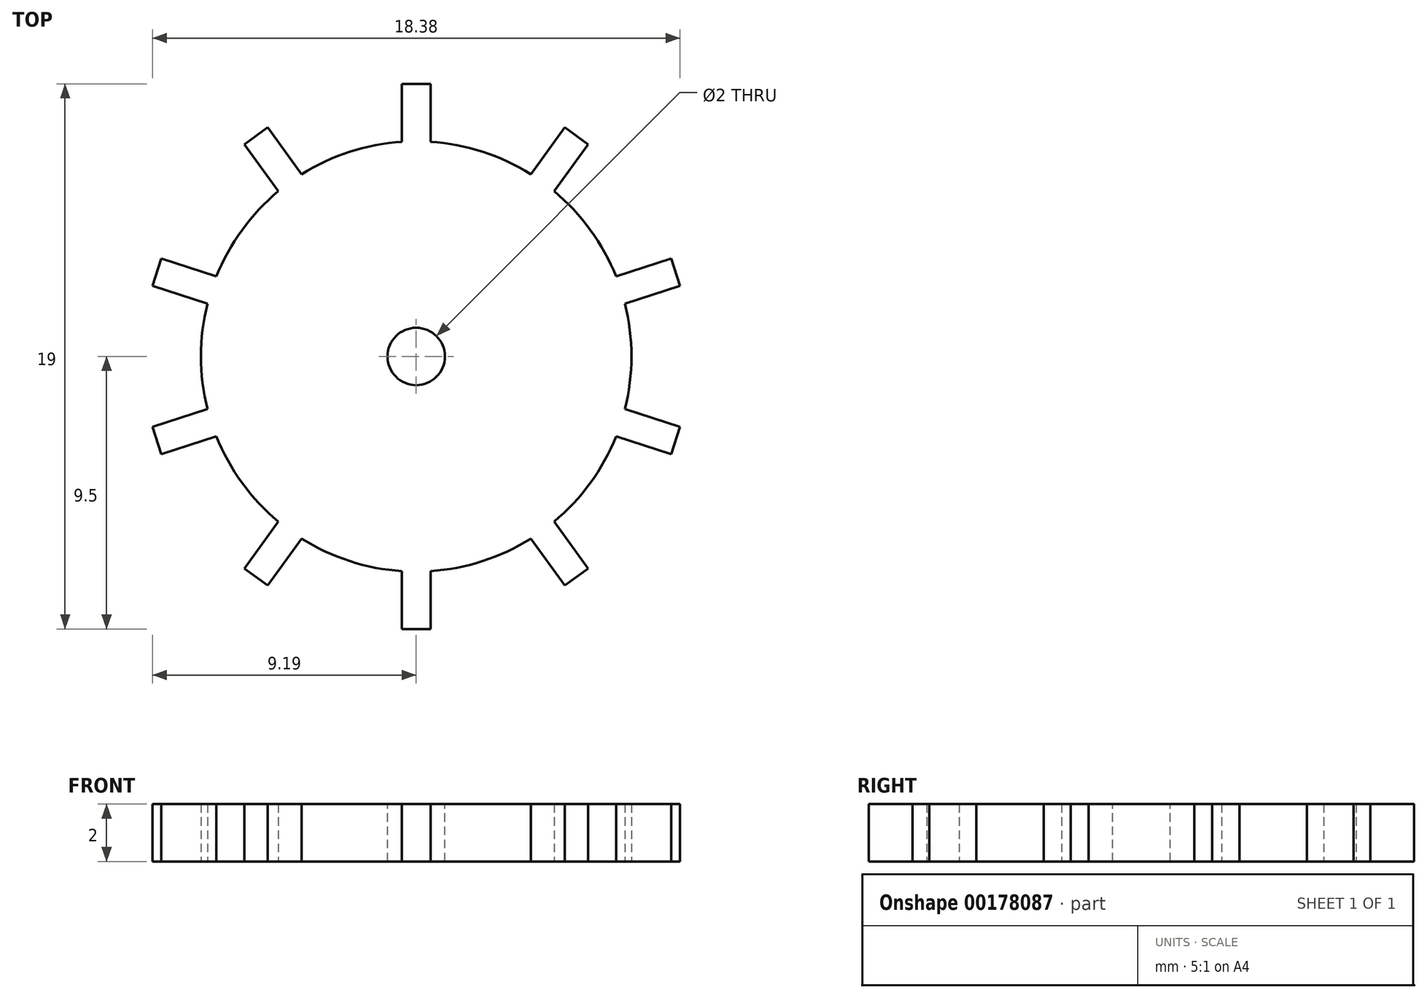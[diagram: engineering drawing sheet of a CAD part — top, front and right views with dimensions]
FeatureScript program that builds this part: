
annotation { "Feature Type Name" : "Feature", "Feature Type Description" : "" }
export const myFeature = defineFeature(function(context is Context, id is Id, definition is map)
    precondition{}
    {
        {
            var Q0;
            Q0=qCreatedBy(makeId("Top.planeOp"),FACE);
            var sketch = newSketch(context, id + "F0", { "sketchPlane" : qUnion([Q0])});
            skCircle(sketch, "E0", {"center": v(0, 0) * mm, "radius": 7.5 * mm});
            skLineSegment(sketch, "E1", {"start": v(0, 0) * mm, "end": v(0, 7.5) * mm, "construction": true});
            skLineSegment(sketch, "E2", {"start": v(0, 9.5) * mm, "end": v(-0.5, 9.5) * mm});
            skLineSegment(sketch, "E3", {"start": v(-0.5, 9.5) * mm, "end": v(-0.5, 7.48) * mm});
            skLineSegment(sketch, "E4.MirrorCS", {"start": v(0, 9.5) * mm, "end": v(0.5, 9.5) * mm});
            skLineSegment(sketch, "E5.MirrorCS", {"start": v(0.5, 9.5) * mm, "end": v(0.5, 7.48) * mm});
            skLineSegment(sketch, "E6.1.0", {"start": v(-5.99, 7.4) * mm, "end": v(-4.8, 5.76) * mm});
            skLineSegment(sketch, "E6.1.1", {"start": v(-5.58, 7.69) * mm, "end": v(-5.99, 7.4) * mm});
            skLineSegment(sketch, "E6.1.2", {"start": v(-5.58, 7.69) * mm, "end": v(-5.18, 7.98) * mm});
            skLineSegment(sketch, "E6.1.3", {"start": v(-5.18, 7.98) * mm, "end": v(-4, 6.35) * mm});
            skLineSegment(sketch, "E6.2.0", {"start": v(-9.19, 2.46) * mm, "end": v(-7.27, 1.84) * mm});
            skLineSegment(sketch, "E6.2.1", {"start": v(-9.04, 2.94) * mm, "end": v(-9.19, 2.46) * mm});
            skLineSegment(sketch, "E6.2.2", {"start": v(-9.04, 2.94) * mm, "end": v(-8.88, 3.41) * mm});
            skLineSegment(sketch, "E6.2.3", {"start": v(-8.88, 3.41) * mm, "end": v(-6.96, 2.79) * mm});
            skLineSegment(sketch, "E6.3.0", {"start": v(-8.88, -3.41) * mm, "end": v(-6.96, -2.79) * mm});
            skLineSegment(sketch, "E6.3.1", {"start": v(-9.04, -2.94) * mm, "end": v(-8.88, -3.41) * mm});
            skLineSegment(sketch, "E6.3.2", {"start": v(-9.04, -2.94) * mm, "end": v(-9.19, -2.46) * mm});
            skLineSegment(sketch, "E6.3.3", {"start": v(-9.19, -2.46) * mm, "end": v(-7.27, -1.84) * mm});
            skLineSegment(sketch, "E6.4.0", {"start": v(-5.18, -7.98) * mm, "end": v(-4, -6.35) * mm});
            skLineSegment(sketch, "E6.4.1", {"start": v(-5.58, -7.69) * mm, "end": v(-5.18, -7.98) * mm});
            skLineSegment(sketch, "E6.4.2", {"start": v(-5.58, -7.69) * mm, "end": v(-5.99, -7.4) * mm});
            skLineSegment(sketch, "E6.4.3", {"start": v(-5.99, -7.4) * mm, "end": v(-4.8, -5.76) * mm});
            skLineSegment(sketch, "E6.5.0", {"start": v(0.5, -9.5) * mm, "end": v(0.5, -7.48) * mm});
            skLineSegment(sketch, "E6.5.1", {"start": v(0, -9.5) * mm, "end": v(0.5, -9.5) * mm});
            skLineSegment(sketch, "E6.5.2", {"start": v(0, -9.5) * mm, "end": v(-0.5, -9.5) * mm});
            skLineSegment(sketch, "E6.5.3", {"start": v(-0.5, -9.5) * mm, "end": v(-0.5, -7.48) * mm});
            skLineSegment(sketch, "E7.2.6.0", {"start": v(5.99, -7.4) * mm, "end": v(4.8, -5.76) * mm});
            skLineSegment(sketch, "E7.3.6.0", {"start": v(5.58, -7.69) * mm, "end": v(5.99, -7.4) * mm});
            skLineSegment(sketch, "E7.6.6.0", {"start": v(5.58, -7.69) * mm, "end": v(5.18, -7.98) * mm});
            skLineSegment(sketch, "E7.9.6.0", {"start": v(5.18, -7.98) * mm, "end": v(4, -6.35) * mm});
            skLineSegment(sketch, "E7.2.7.0", {"start": v(9.19, -2.46) * mm, "end": v(7.27, -1.84) * mm});
            skLineSegment(sketch, "E7.3.7.0", {"start": v(9.04, -2.94) * mm, "end": v(9.19, -2.46) * mm});
            skLineSegment(sketch, "E7.6.7.0", {"start": v(9.04, -2.94) * mm, "end": v(8.88, -3.41) * mm});
            skLineSegment(sketch, "E7.9.7.0", {"start": v(8.88, -3.41) * mm, "end": v(6.96, -2.79) * mm});
            skLineSegment(sketch, "E7.2.8.0", {"start": v(8.88, 3.41) * mm, "end": v(6.96, 2.79) * mm});
            skLineSegment(sketch, "E7.3.8.0", {"start": v(9.04, 2.94) * mm, "end": v(8.88, 3.41) * mm});
            skLineSegment(sketch, "E7.6.8.0", {"start": v(9.04, 2.94) * mm, "end": v(9.19, 2.46) * mm});
            skLineSegment(sketch, "E7.9.8.0", {"start": v(9.19, 2.46) * mm, "end": v(7.27, 1.84) * mm});
            skLineSegment(sketch, "E7.2.9.0", {"start": v(5.18, 7.98) * mm, "end": v(4, 6.35) * mm});
            skLineSegment(sketch, "E7.3.9.0", {"start": v(5.58, 7.69) * mm, "end": v(5.18, 7.98) * mm});
            skLineSegment(sketch, "E7.6.9.0", {"start": v(5.58, 7.69) * mm, "end": v(5.99, 7.4) * mm});
            skLineSegment(sketch, "E7.9.9.0", {"start": v(5.99, 7.4) * mm, "end": v(4.8, 5.76) * mm});
            skSolve(sketch);
        }
        {
            var Q0;
            Q0 = qSketchRegion(id + "F0", true);
            extrude(context, id + "F1", {"entities" : qUnion([Q0]), "depth" : 2 * mm});
        }
        {
            var Q0;
            Q0=makeQuery(id+"F1.opExtrude","CAP_FACE",FACE,{"disambiguationData":[OSD([sQuery(id+"F0.wireOp",EDGE,"E0"),sQuery(id+"F0.wireOp",EDGE,"E2"),sQuery(id+"F0.wireOp",EDGE,"E3"),sQuery(id+"F0.wireOp",EDGE,"E4.MirrorCS"),sQuery(id+"F0.wireOp",EDGE,"E5.MirrorCS"),sQuery(id+"F0.wireOp",EDGE,"E6.1.0"),sQuery(id+"F0.wireOp",EDGE,"E6.1.1"),sQuery(id+"F0.wireOp",EDGE,"E6.1.2"),sQuery(id+"F0.wireOp",EDGE,"E6.1.3"),sQuery(id+"F0.wireOp",EDGE,"E6.2.0"),sQuery(id+"F0.wireOp",EDGE,"E6.2.1"),sQuery(id+"F0.wireOp",EDGE,"E6.2.2"),sQuery(id+"F0.wireOp",EDGE,"E6.2.3"),sQuery(id+"F0.wireOp",EDGE,"E6.3.0"),sQuery(id+"F0.wireOp",EDGE,"E6.3.1"),sQuery(id+"F0.wireOp",EDGE,"E6.3.2"),sQuery(id+"F0.wireOp",EDGE,"E6.3.3"),sQuery(id+"F0.wireOp",EDGE,"E6.4.0"),sQuery(id+"F0.wireOp",EDGE,"E6.4.1"),sQuery(id+"F0.wireOp",EDGE,"E6.4.2"),sQuery(id+"F0.wireOp",EDGE,"E6.4.3"),sQuery(id+"F0.wireOp",EDGE,"E6.5.0"),sQuery(id+"F0.wireOp",EDGE,"E6.5.1"),sQuery(id+"F0.wireOp",EDGE,"E6.5.2"),sQuery(id+"F0.wireOp",EDGE,"E6.5.3")])],"isStart":false});
            var sketch = newSketch(context, id + "F2", { "sketchPlane" : qUnion([Q0])});
            skCircle(sketch, "E8", {"center": v(0, 0) * mm, "radius": 1 * mm});
            skSolve(sketch);
        }
        {
            var Q0;
            Q0 = qSketchRegion(id + "F2", true);
            extrude(context, id + "F3", {"entities" : qUnion([Q0]), "operationType" : NewBodyOperationType.REMOVE, "endBound" : BoundingType.THROUGH_ALL, "oppositeDirection" : true, "depth" : 25 * mm});
        }
    });
